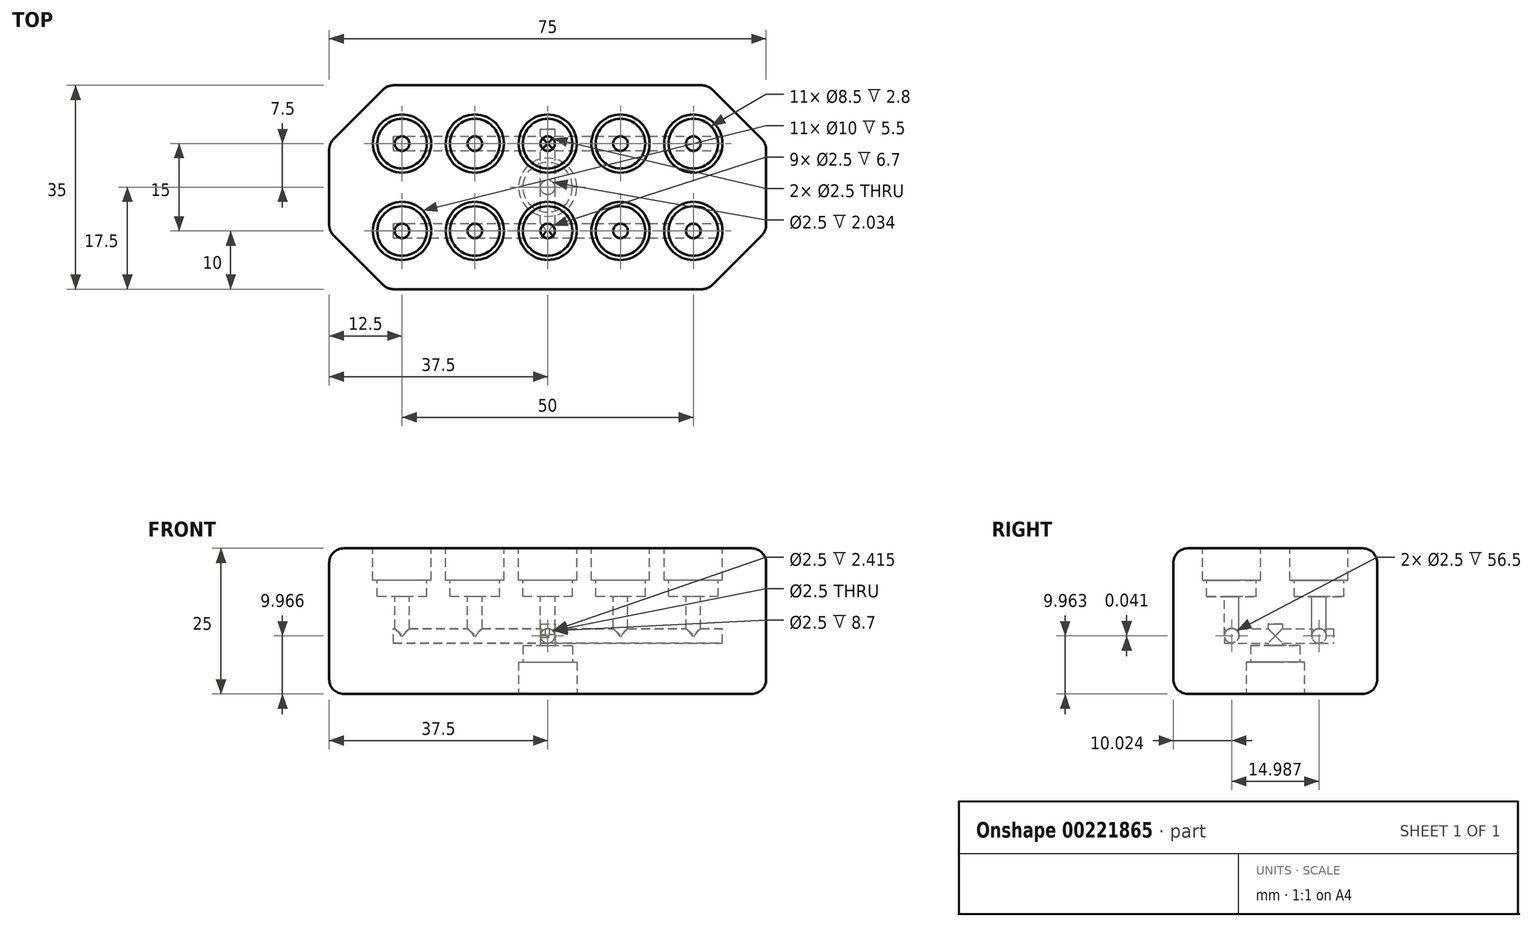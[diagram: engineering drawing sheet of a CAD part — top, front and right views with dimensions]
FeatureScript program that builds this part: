
annotation { "Feature Type Name" : "Feature", "Feature Type Description" : "" }
export const myFeature = defineFeature(function(context is Context, id is Id, definition is map)
    precondition{}
    {
        {
            var Q0;
            Q0=qCreatedBy(makeId("Top.planeOp"),FACE);
            var sketch = newSketch(context, id + "F0", { "sketchPlane" : qUnion([Q0])});
            skLineSegment(sketch, "E0.bottom", {"start": v(-37.5, 17.5) * mm, "end": v(37.5, 17.5) * mm});
            skLineSegment(sketch, "E0.top", {"start": v(-37.5, -17.5) * mm, "end": v(37.5, -17.5) * mm});
            skLineSegment(sketch, "E0.left", {"start": v(-37.5, 17.5) * mm, "end": v(-37.5, -17.5) * mm});
            skLineSegment(sketch, "E0.right", {"start": v(37.5, 17.5) * mm, "end": v(37.5, -17.5) * mm});
            skPoint(sketch, "E0.middle", {"position": v(0, 0) * mm});
            skSolve(sketch);
        }
        {
            var Q0;
            Q0=makeQuery(id+"F0.imprint","IMPRINT",FACE,{"disambiguationData":[TD([[makeQuery(id+"F0.imprint","IMPRINT",EDGE,{"derivedFrom":sQuery(id+"F0.wireOp",EDGE,"E0.bottom")}),-1.0]])]});
            extrude(context, id + "F1", {"entities" : qUnion([Q0]), "depth" : 25 * mm});
        }
        {
            var Q0;
            Q0=makeQuery(id+"F1.opExtrude","CAP_FACE",FACE,{"disambiguationData":[OSD([sQuery(id+"F0.wireOp",EDGE,"E0.bottom"),sQuery(id+"F0.wireOp",EDGE,"E0.top"),sQuery(id+"F0.wireOp",EDGE,"E0.left"),sQuery(id+"F0.wireOp",EDGE,"E0.right")])],"isStart":false});
            var sketch = newSketch(context, id + "F2", { "sketchPlane" : qUnion([Q0])});
            skCircle(sketch, "E1", {"center": v(-25, 7.5) * mm, "radius": 5 * mm});
            skCircle(sketch, "E2", {"center": v(-25, -7.5) * mm, "radius": 5 * mm});
            skCircle(sketch, "E3", {"center": v(-12.5, 7.5) * mm, "radius": 5 * mm});
            skCircle(sketch, "E4", {"center": v(-12.5, -7.5) * mm, "radius": 5 * mm});
            skCircle(sketch, "E5", {"center": v(0, 7.5) * mm, "radius": 5 * mm});
            skCircle(sketch, "E6", {"center": v(12.5, -7.5) * mm, "radius": 5 * mm});
            skCircle(sketch, "E7", {"center": v(0, -7.5) * mm, "radius": 5 * mm});
            skCircle(sketch, "E8", {"center": v(12.5, 7.5) * mm, "radius": 5 * mm});
            skCircle(sketch, "E9", {"center": v(25, -7.5) * mm, "radius": 5 * mm});
            skCircle(sketch, "E10", {"center": v(25, 7.5) * mm, "radius": 5 * mm});
            skCircle(sketch, "E11", {"center": v(-25, 7.5) * mm, "radius": 4.25 * mm});
            skCircle(sketch, "E12", {"center": v(-12.5, 7.5) * mm, "radius": 4.25 * mm});
            skCircle(sketch, "E13", {"center": v(0, 7.5) * mm, "radius": 4.25 * mm});
            skCircle(sketch, "E14", {"center": v(12.5, 7.5) * mm, "radius": 4.25 * mm});
            skCircle(sketch, "E15", {"center": v(25, 7.5) * mm, "radius": 4.25 * mm});
            skCircle(sketch, "E16", {"center": v(25, -7.5) * mm, "radius": 4.25 * mm});
            skCircle(sketch, "E17", {"center": v(12.5, -7.5) * mm, "radius": 4.25 * mm});
            skCircle(sketch, "E18", {"center": v(0, -7.5) * mm, "radius": 4.25 * mm});
            skCircle(sketch, "E19", {"center": v(-12.5, -7.5) * mm, "radius": 4.25 * mm});
            skCircle(sketch, "E20", {"center": v(-25, -7.5) * mm, "radius": 4.25 * mm});
            skCircle(sketch, "E21", {"center": v(-25, 7.5) * mm, "radius": 1.25 * mm});
            skCircle(sketch, "E22", {"center": v(-12.5, 7.5) * mm, "radius": 1.25 * mm});
            skCircle(sketch, "E23", {"center": v(0, 7.5) * mm, "radius": 1.25 * mm});
            skCircle(sketch, "E24", {"center": v(12.5, 7.5) * mm, "radius": 1.25 * mm});
            skCircle(sketch, "E25", {"center": v(25, 7.5) * mm, "radius": 1.25 * mm});
            skCircle(sketch, "E26", {"center": v(25, -7.5) * mm, "radius": 1.25 * mm});
            skCircle(sketch, "E27", {"center": v(0, -7.5) * mm, "radius": 1.25 * mm});
            skCircle(sketch, "E28", {"center": v(-25, -7.5) * mm, "radius": 1.25 * mm});
            skCircle(sketch, "E29", {"center": v(-12.5, -7.5) * mm, "radius": 1.25 * mm});
            skCircle(sketch, "E30", {"center": v(12.5, -7.5) * mm, "radius": 1.25 * mm});
            skSolve(sketch);
        }
        {
            var Q0;
            Q0=makeQuery(id+"F1.opExtrude","CAP_FACE",FACE,{"disambiguationData":[OSD([sQuery(id+"F0.wireOp",EDGE,"E0.bottom"),sQuery(id+"F0.wireOp",EDGE,"E0.top"),sQuery(id+"F0.wireOp",EDGE,"E0.left"),sQuery(id+"F0.wireOp",EDGE,"E0.right")])],"isStart":true});
            var sketch = newSketch(context, id + "F3", { "sketchPlane" : qUnion([Q0])});
            skCircle(sketch, "E31", {"center": v(0, 0) * mm, "radius": 5 * mm});
            skCircle(sketch, "E32", {"center": v(0, 0) * mm, "radius": 4.25 * mm});
            skCircle(sketch, "E33", {"center": v(0, 0) * mm, "radius": 1.25 * mm});
            skSolve(sketch);
        }
        {
            var Q0;
            Q0=makeQuery(id+"F2.imprint","IMPRINT",FACE,{"disambiguationData":[TD([[makeQuery(id+"F2.imprint","IMPRINT",EDGE,{"derivedFrom":sQuery(id+"F2.wireOp",EDGE,"E11")}),1.0]])]});
            var Q1;
            Q1=makeQuery(id+"F2.imprint","IMPRINT",FACE,{"disambiguationData":[TD([[makeQuery(id+"F2.imprint","IMPRINT",EDGE,{"derivedFrom":sQuery(id+"F2.wireOp",EDGE,"E12")}),1.0]])]});
            var Q2;
            Q2=makeQuery(id+"F2.imprint","IMPRINT",FACE,{"disambiguationData":[TD([[makeQuery(id+"F2.imprint","IMPRINT",EDGE,{"derivedFrom":sQuery(id+"F2.wireOp",EDGE,"E13")}),1.0]])]});
            var Q3;
            Q3=makeQuery(id+"F2.imprint","IMPRINT",FACE,{"disambiguationData":[TD([[makeQuery(id+"F2.imprint","IMPRINT",EDGE,{"derivedFrom":sQuery(id+"F2.wireOp",EDGE,"E14")}),1.0]])]});
            var Q4;
            Q4=makeQuery(id+"F2.imprint","IMPRINT",FACE,{"disambiguationData":[TD([[makeQuery(id+"F2.imprint","IMPRINT",EDGE,{"derivedFrom":sQuery(id+"F2.wireOp",EDGE,"E15")}),1.0]])]});
            var Q5;
            Q5=makeQuery(id+"F2.imprint","IMPRINT",FACE,{"disambiguationData":[TD([[makeQuery(id+"F2.imprint","IMPRINT",EDGE,{"derivedFrom":sQuery(id+"F2.wireOp",EDGE,"E20")}),1.0]])]});
            var Q6;
            Q6=makeQuery(id+"F2.imprint","IMPRINT",FACE,{"disambiguationData":[TD([[makeQuery(id+"F2.imprint","IMPRINT",EDGE,{"derivedFrom":sQuery(id+"F2.wireOp",EDGE,"E19")}),1.0]])]});
            var Q7;
            Q7=makeQuery(id+"F2.imprint","IMPRINT",FACE,{"disambiguationData":[TD([[makeQuery(id+"F2.imprint","IMPRINT",EDGE,{"derivedFrom":sQuery(id+"F2.wireOp",EDGE,"E18")}),1.0]])]});
            var Q8;
            Q8=makeQuery(id+"F2.imprint","IMPRINT",FACE,{"disambiguationData":[TD([[makeQuery(id+"F2.imprint","IMPRINT",EDGE,{"derivedFrom":sQuery(id+"F2.wireOp",EDGE,"E17")}),1.0]])]});
            var Q9;
            Q9=makeQuery(id+"F2.imprint","IMPRINT",FACE,{"disambiguationData":[TD([[makeQuery(id+"F2.imprint","IMPRINT",EDGE,{"derivedFrom":sQuery(id+"F2.wireOp",EDGE,"E16")}),1.0]])]});
            extrude(context, id + "F4", {"entities" : qUnion([Q0, Q1, Q2, Q3, Q4, Q5, Q6, Q7, Q8, Q9]), "operationType" : NewBodyOperationType.REMOVE, "oppositeDirection" : true, "depth" : 8.3 * mm});
        }
        {
            var Q0;
            Q0=makeQuery(id+"F4.boolean.opBoolean","SPLIT",FACE,{"disambiguationData":[TD([makeQuery(id+"F4.opExtrude","SWEPT_FACE",FACE,{"disambiguationData":[OSD([sQuery(id+"F2.wireOp",EDGE,"E21")])]})])],"derivedFrom":makeQuery(id+"F1.opExtrude","CAP_FACE",FACE,{"disambiguationData":[OSD([sQuery(id+"F0.wireOp",EDGE,"E0.bottom"),sQuery(id+"F0.wireOp",EDGE,"E0.top"),sQuery(id+"F0.wireOp",EDGE,"E0.left"),sQuery(id+"F0.wireOp",EDGE,"E0.right")])],"isStart":false})});
            var Q1;
            Q1=makeQuery(id+"F4.boolean.opBoolean","SPLIT",FACE,{"disambiguationData":[TD([makeQuery(id+"F4.opExtrude","SWEPT_FACE",FACE,{"disambiguationData":[OSD([sQuery(id+"F2.wireOp",EDGE,"E22")])]})])],"derivedFrom":makeQuery(id+"F1.opExtrude","CAP_FACE",FACE,{"disambiguationData":[OSD([sQuery(id+"F0.wireOp",EDGE,"E0.bottom"),sQuery(id+"F0.wireOp",EDGE,"E0.top"),sQuery(id+"F0.wireOp",EDGE,"E0.left"),sQuery(id+"F0.wireOp",EDGE,"E0.right")])],"isStart":false})});
            var Q2;
            Q2=makeQuery(id+"F4.boolean.opBoolean","SPLIT",FACE,{"disambiguationData":[TD([makeQuery(id+"F4.opExtrude","SWEPT_FACE",FACE,{"disambiguationData":[OSD([sQuery(id+"F2.wireOp",EDGE,"E23")])]})])],"derivedFrom":makeQuery(id+"F1.opExtrude","CAP_FACE",FACE,{"disambiguationData":[OSD([sQuery(id+"F0.wireOp",EDGE,"E0.bottom"),sQuery(id+"F0.wireOp",EDGE,"E0.top"),sQuery(id+"F0.wireOp",EDGE,"E0.left"),sQuery(id+"F0.wireOp",EDGE,"E0.right")])],"isStart":false})});
            var Q3;
            Q3=makeQuery(id+"F4.boolean.opBoolean","SPLIT",FACE,{"disambiguationData":[TD([makeQuery(id+"F4.opExtrude","SWEPT_FACE",FACE,{"disambiguationData":[OSD([sQuery(id+"F2.wireOp",EDGE,"E24")])]})])],"derivedFrom":makeQuery(id+"F1.opExtrude","CAP_FACE",FACE,{"disambiguationData":[OSD([sQuery(id+"F0.wireOp",EDGE,"E0.bottom"),sQuery(id+"F0.wireOp",EDGE,"E0.top"),sQuery(id+"F0.wireOp",EDGE,"E0.left"),sQuery(id+"F0.wireOp",EDGE,"E0.right")])],"isStart":false})});
            var Q4;
            Q4=makeQuery(id+"F4.boolean.opBoolean","SPLIT",FACE,{"disambiguationData":[TD([makeQuery(id+"F4.opExtrude","SWEPT_FACE",FACE,{"disambiguationData":[OSD([sQuery(id+"F2.wireOp",EDGE,"E25")])]})])],"derivedFrom":makeQuery(id+"F1.opExtrude","CAP_FACE",FACE,{"disambiguationData":[OSD([sQuery(id+"F0.wireOp",EDGE,"E0.bottom"),sQuery(id+"F0.wireOp",EDGE,"E0.top"),sQuery(id+"F0.wireOp",EDGE,"E0.left"),sQuery(id+"F0.wireOp",EDGE,"E0.right")])],"isStart":false})});
            var Q5;
            Q5=makeQuery(id+"F4.boolean.opBoolean","SPLIT",FACE,{"disambiguationData":[TD([makeQuery(id+"F4.opExtrude","SWEPT_FACE",FACE,{"disambiguationData":[OSD([sQuery(id+"F2.wireOp",EDGE,"E28")])]})])],"derivedFrom":makeQuery(id+"F1.opExtrude","CAP_FACE",FACE,{"disambiguationData":[OSD([sQuery(id+"F0.wireOp",EDGE,"E0.bottom"),sQuery(id+"F0.wireOp",EDGE,"E0.top"),sQuery(id+"F0.wireOp",EDGE,"E0.left"),sQuery(id+"F0.wireOp",EDGE,"E0.right")])],"isStart":false})});
            var Q6;
            Q6=makeQuery(id+"F4.boolean.opBoolean","SPLIT",FACE,{"disambiguationData":[TD([makeQuery(id+"F4.opExtrude","SWEPT_FACE",FACE,{"disambiguationData":[OSD([sQuery(id+"F2.wireOp",EDGE,"E29")])]})])],"derivedFrom":makeQuery(id+"F1.opExtrude","CAP_FACE",FACE,{"disambiguationData":[OSD([sQuery(id+"F0.wireOp",EDGE,"E0.bottom"),sQuery(id+"F0.wireOp",EDGE,"E0.top"),sQuery(id+"F0.wireOp",EDGE,"E0.left"),sQuery(id+"F0.wireOp",EDGE,"E0.right")])],"isStart":false})});
            var Q7;
            Q7=makeQuery(id+"F4.boolean.opBoolean","SPLIT",FACE,{"disambiguationData":[TD([makeQuery(id+"F4.opExtrude","SWEPT_FACE",FACE,{"disambiguationData":[OSD([sQuery(id+"F2.wireOp",EDGE,"E27")])]})])],"derivedFrom":makeQuery(id+"F1.opExtrude","CAP_FACE",FACE,{"disambiguationData":[OSD([sQuery(id+"F0.wireOp",EDGE,"E0.bottom"),sQuery(id+"F0.wireOp",EDGE,"E0.top"),sQuery(id+"F0.wireOp",EDGE,"E0.left"),sQuery(id+"F0.wireOp",EDGE,"E0.right")])],"isStart":false})});
            var Q8;
            Q8=makeQuery(id+"F4.boolean.opBoolean","SPLIT",FACE,{"disambiguationData":[TD([makeQuery(id+"F4.opExtrude","SWEPT_FACE",FACE,{"disambiguationData":[OSD([sQuery(id+"F2.wireOp",EDGE,"E30")])]})])],"derivedFrom":makeQuery(id+"F1.opExtrude","CAP_FACE",FACE,{"disambiguationData":[OSD([sQuery(id+"F0.wireOp",EDGE,"E0.bottom"),sQuery(id+"F0.wireOp",EDGE,"E0.top"),sQuery(id+"F0.wireOp",EDGE,"E0.left"),sQuery(id+"F0.wireOp",EDGE,"E0.right")])],"isStart":false})});
            var Q9;
            Q9=makeQuery(id+"F4.boolean.opBoolean","SPLIT",FACE,{"disambiguationData":[TD([makeQuery(id+"F4.opExtrude","SWEPT_FACE",FACE,{"disambiguationData":[OSD([sQuery(id+"F2.wireOp",EDGE,"E26")])]})])],"derivedFrom":makeQuery(id+"F1.opExtrude","CAP_FACE",FACE,{"disambiguationData":[OSD([sQuery(id+"F0.wireOp",EDGE,"E0.bottom"),sQuery(id+"F0.wireOp",EDGE,"E0.top"),sQuery(id+"F0.wireOp",EDGE,"E0.left"),sQuery(id+"F0.wireOp",EDGE,"E0.right")])],"isStart":false})});
            extrude(context, id + "F5", {"entities" : qUnion([Q0, Q1, Q2, Q3, Q4, Q5, Q6, Q7, Q8, Q9]), "operationType" : NewBodyOperationType.REMOVE, "oppositeDirection" : true, "depth" : 15 * mm});
        }
        {
            var Q0;
            Q0=makeQuery(id+"F2.imprint","IMPRINT",FACE,{"disambiguationData":[TD([[makeQuery(id+"F2.imprint","IMPRINT",EDGE,{"derivedFrom":sQuery(id+"F2.wireOp",EDGE,"E1")}),1.0]])]});
            var Q1;
            Q1=makeQuery(id+"F2.imprint","IMPRINT",FACE,{"disambiguationData":[TD([[makeQuery(id+"F2.imprint","IMPRINT",EDGE,{"derivedFrom":sQuery(id+"F2.wireOp",EDGE,"E3")}),1.0]])]});
            var Q2;
            Q2=makeQuery(id+"F2.imprint","IMPRINT",FACE,{"disambiguationData":[TD([[makeQuery(id+"F2.imprint","IMPRINT",EDGE,{"derivedFrom":sQuery(id+"F2.wireOp",EDGE,"E2")}),1.0]])]});
            var Q3;
            Q3=makeQuery(id+"F2.imprint","IMPRINT",FACE,{"disambiguationData":[TD([[makeQuery(id+"F2.imprint","IMPRINT",EDGE,{"derivedFrom":sQuery(id+"F2.wireOp",EDGE,"E4")}),1.0]])]});
            var Q4;
            Q4=makeQuery(id+"F2.imprint","IMPRINT",FACE,{"disambiguationData":[TD([[makeQuery(id+"F2.imprint","IMPRINT",EDGE,{"derivedFrom":sQuery(id+"F2.wireOp",EDGE,"E7")}),1.0]])]});
            var Q5;
            Q5=makeQuery(id+"F2.imprint","IMPRINT",FACE,{"disambiguationData":[TD([[makeQuery(id+"F2.imprint","IMPRINT",EDGE,{"derivedFrom":sQuery(id+"F2.wireOp",EDGE,"E6")}),1.0]])]});
            var Q6;
            Q6=makeQuery(id+"F2.imprint","IMPRINT",FACE,{"disambiguationData":[TD([[makeQuery(id+"F2.imprint","IMPRINT",EDGE,{"derivedFrom":sQuery(id+"F2.wireOp",EDGE,"E9")}),1.0]])]});
            var Q7;
            Q7=makeQuery(id+"F2.imprint","IMPRINT",FACE,{"disambiguationData":[TD([[makeQuery(id+"F2.imprint","IMPRINT",EDGE,{"derivedFrom":sQuery(id+"F2.wireOp",EDGE,"E5")}),1.0]])]});
            var Q8;
            Q8=makeQuery(id+"F2.imprint","IMPRINT",FACE,{"disambiguationData":[TD([[makeQuery(id+"F2.imprint","IMPRINT",EDGE,{"derivedFrom":sQuery(id+"F2.wireOp",EDGE,"E8")}),1.0]])]});
            var Q9;
            Q9=makeQuery(id+"F2.imprint","IMPRINT",FACE,{"disambiguationData":[TD([[makeQuery(id+"F2.imprint","IMPRINT",EDGE,{"derivedFrom":sQuery(id+"F2.wireOp",EDGE,"E10")}),1.0]])]});
            extrude(context, id + "F6", {"entities" : qUnion([Q0, Q1, Q2, Q3, Q4, Q5, Q6, Q7, Q8, Q9]), "operationType" : NewBodyOperationType.REMOVE, "oppositeDirection" : true, "depth" : 5.5 * mm});
        }
        {
            var Q0;
            Q0=makeQuery(id+"F3.imprint","IMPRINT",FACE,{"disambiguationData":[TD([[makeQuery(id+"F3.imprint","IMPRINT",EDGE,{"derivedFrom":sQuery(id+"F3.wireOp",EDGE,"E32")}),1.0]])]});
            extrude(context, id + "F7", {"entities" : qUnion([Q0]), "operationType" : NewBodyOperationType.REMOVE, "oppositeDirection" : true, "depth" : 8.3 * mm});
        }
        {
            var Q0;
            Q0=makeQuery(id+"F7.boolean.opBoolean","SPLIT",FACE,{"disambiguationData":[TD([makeQuery(id+"F7.opExtrude","SWEPT_FACE",FACE,{"disambiguationData":[OSD([sQuery(id+"F3.wireOp",EDGE,"E33")])]})])],"derivedFrom":makeQuery(id+"F1.opExtrude","CAP_FACE",FACE,{"disambiguationData":[OSD([sQuery(id+"F0.wireOp",EDGE,"E0.bottom"),sQuery(id+"F0.wireOp",EDGE,"E0.top"),sQuery(id+"F0.wireOp",EDGE,"E0.left"),sQuery(id+"F0.wireOp",EDGE,"E0.right")])],"isStart":true})});
            extrude(context, id + "F8", {"entities" : qUnion([Q0]), "operationType" : NewBodyOperationType.REMOVE, "oppositeDirection" : true, "depth" : 12 * mm});
        }
        {
            var Q0;
            Q0=makeQuery(id+"F3.imprint","IMPRINT",FACE,{"disambiguationData":[TD([[makeQuery(id+"F3.imprint","IMPRINT",EDGE,{"derivedFrom":sQuery(id+"F3.wireOp",EDGE,"E31")}),1.0]])]});
            extrude(context, id + "F9", {"entities" : qUnion([Q0]), "operationType" : NewBodyOperationType.REMOVE, "oppositeDirection" : true, "depth" : 5.5 * mm});
        }
        {
            var Q0;
            Q0=makeQuery(id+"F1.opExtrude","SWEPT_FACE",FACE,{"disambiguationData":[OSD([sQuery(id+"F0.wireOp",EDGE,"E0.right")])]});
            var sketch = newSketch(context, id + "F10", { "sketchPlane" : qUnion([Q0])});
            skCircle(sketch, "E34", {"center": v(-7.48, 10) * mm, "radius": 1.25 * mm});
            skCircle(sketch, "E35", {"center": v(7.51, 9.96) * mm, "radius": 1.25 * mm});
            skSolve(sketch);
        }
        {
            var Q0;
            Q0=makeQuery(id+"F10.imprint","IMPRINT",FACE,{"disambiguationData":[TD([[makeQuery(id+"F10.imprint","IMPRINT",EDGE,{"derivedFrom":sQuery(id+"F10.wireOp",EDGE,"E35")}),1.0]])]});
            var Q1;
            Q1=makeQuery(id+"F10.imprint","IMPRINT",FACE,{"disambiguationData":[TD([[makeQuery(id+"F10.imprint","IMPRINT",EDGE,{"derivedFrom":sQuery(id+"F10.wireOp",EDGE,"E34")}),1.0]])]});
            extrude(context, id + "F11", {"entities" : qUnion([Q0, Q1]), "operationType" : NewBodyOperationType.REMOVE, "oppositeDirection" : true, "depth" : 64 * mm});
        }
        {
            var Q0;
            Q0=makeQuery(id+"F1.opExtrude","SWEPT_FACE",FACE,{"disambiguationData":[OSD([sQuery(id+"F0.wireOp",EDGE,"E0.bottom")])]});
            var sketch = newSketch(context, id + "F12", { "sketchPlane" : qUnion([Q0])});
            skCircle(sketch, "E36", {"center": v(0, 9.97) * mm, "radius": 1.25 * mm});
            skSolve(sketch);
        }
        {
            var Q0;
            Q0=makeQuery(id+"F12.imprint","IMPRINT",FACE,{"disambiguationData":[TD([[makeQuery(id+"F12.imprint","IMPRINT",EDGE,{"derivedFrom":sQuery(id+"F12.wireOp",EDGE,"E36")}),1.0]])]});
            extrude(context, id + "F13", {"entities" : qUnion([Q0]), "operationType" : NewBodyOperationType.REMOVE, "oppositeDirection" : true, "depth" : 26.2 * mm});
        }
        {
            var Q0;
            Q0=makeQuery(id+"F1.opExtrude","SWEPT_FACE",FACE,{"disambiguationData":[OSD([sQuery(id+"F0.wireOp",EDGE,"E0.right")])]});
            var sketch = newSketch(context, id + "F14", { "sketchPlane" : qUnion([Q0])});
            skCircle(sketch, "E37", {"center": v(-7.48, 10) * mm, "radius": 1.25 * mm});
            skCircle(sketch, "E38", {"center": v(7.51, 9.96) * mm, "radius": 1.25 * mm});
            skSolve(sketch);
        }
        {
            var Q0;
            Q0 = qSketchRegion(id + "F14", true);
            extrude(context, id + "F15", {"entities" : qUnion([Q0]), "operationType" : NewBodyOperationType.ADD, "oppositeDirection" : true, "depth" : 7.5 * mm});
        }
        {
            var Q0;
            Q0=makeQuery(id+"F1.opExtrude","SWEPT_FACE",FACE,{"disambiguationData":[OSD([sQuery(id+"F0.wireOp",EDGE,"E0.bottom")])]});
            var sketch = newSketch(context, id + "F16", { "sketchPlane" : qUnion([Q0])});
            skCircle(sketch, "E39", {"center": v(0, 9.97) * mm, "radius": 1.25 * mm});
            skSolve(sketch);
        }
        {
            var Q0;
            Q0 = qSketchRegion(id + "F16", true);
            extrude(context, id + "F17", {"entities" : qUnion([Q0]), "operationType" : NewBodyOperationType.ADD, "oppositeDirection" : true, "depth" : 7.5 * mm});
        }
        {
            var Q0;
            Q0=makeQuery(id+"F1.opExtrude","SWEPT_EDGE",EDGE,{"disambiguationData":[OSD([sQuery(id+"F0.wireOp",EDGE,"E0.bottom"),sQuery(id+"F0.wireOp",EDGE,"E0.left")])]});
            var Q1;
            Q1=makeQuery(id+"F1.opExtrude","SWEPT_EDGE",EDGE,{"disambiguationData":[OSD([sQuery(id+"F0.wireOp",EDGE,"E0.top"),sQuery(id+"F0.wireOp",EDGE,"E0.left")])]});
            var Q2;
            Q2=makeQuery(id+"F1.opExtrude","SWEPT_EDGE",EDGE,{"disambiguationData":[OSD([sQuery(id+"F0.wireOp",EDGE,"E0.top"),sQuery(id+"F0.wireOp",EDGE,"E0.right")])]});
            var Q3;
            Q3=makeQuery(id+"F1.opExtrude","SWEPT_EDGE",EDGE,{"disambiguationData":[OSD([sQuery(id+"F0.wireOp",EDGE,"E0.bottom"),sQuery(id+"F0.wireOp",EDGE,"E0.right")])]});
            chamfer(context, id + "F18", {"entities" : qUnion([Q0, Q1, Q2, Q3]), "width" : 10 * mm, "tangentPropagation" : true});
        }
        {
            var Q0;
            {var subQ0=sQuery(id+"F0.wireOp",EDGE,"E0.left");Q0=makeQuery(id+"F18.opChamfer","BLEND_EDGE",EDGE,{"blendedFrom":[makeQuery(id+"F1.opExtrude","SWEPT_EDGE",EDGE,{"disambiguationData":[OSD([sQuery(id+"F0.wireOp",EDGE,"E0.bottom"),subQ0])]}),makeQuery(id+"F1.opExtrude","SWEPT_FACE",FACE,{"disambiguationData":[OSD([subQ0])]})],"blendedInto":[makeQuery(id+"F1.opExtrude","SWEPT_FACE",FACE,{"disambiguationData":[OSD([subQ0])]})]});}
            var Q1;
            {var subQ0=sQuery(id+"F0.wireOp",EDGE,"E0.left");Q1=makeQuery(id+"F18.opChamfer","BLEND_EDGE",EDGE,{"blendedFrom":[makeQuery(id+"F1.opExtrude","SWEPT_EDGE",EDGE,{"disambiguationData":[OSD([sQuery(id+"F0.wireOp",EDGE,"E0.top"),subQ0])]}),makeQuery(id+"F1.opExtrude","SWEPT_FACE",FACE,{"disambiguationData":[OSD([subQ0])]})],"blendedInto":[makeQuery(id+"F1.opExtrude","SWEPT_FACE",FACE,{"disambiguationData":[OSD([subQ0])]})]});}
            var Q2;
            {var subQ0=sQuery(id+"F0.wireOp",EDGE,"E0.bottom");var subQ1=sQuery(id+"F0.wireOp",EDGE,"E0.top");var subQ2=sQuery(id+"F0.wireOp",EDGE,"E0.left");var subQ3=sQuery(id+"F0.wireOp",EDGE,"E0.right");Q2=makeQuery(id+"F18.opChamfer","BLEND_EDGE",EDGE,{"blendedFrom":[makeQuery(id+"F1.opExtrude","SWEPT_EDGE",EDGE,{"disambiguationData":[OSD([subQ1,subQ3])]}),makeQuery(id+"F4.boolean.opBoolean","SPLIT",FACE,{"disambiguationData":[TD([makeQuery(id+"F1.opExtrude","SWEPT_FACE",FACE,{"disambiguationData":[OSD([subQ0])]})])],"derivedFrom":makeQuery(id+"F1.opExtrude","CAP_FACE",FACE,{"disambiguationData":[OSD([subQ0,subQ1,subQ2,subQ3])],"isStart":false})})],"blendedInto":[makeQuery(id+"F4.boolean.opBoolean","SPLIT",FACE,{"disambiguationData":[TD([makeQuery(id+"F1.opExtrude","SWEPT_FACE",FACE,{"disambiguationData":[OSD([subQ0])]})])],"derivedFrom":makeQuery(id+"F1.opExtrude","CAP_FACE",FACE,{"disambiguationData":[OSD([subQ0,subQ1,subQ2,subQ3])],"isStart":false})})]});}
            var Q3;
            {var subQ0=sQuery(id+"F0.wireOp",EDGE,"E0.bottom");Q3=makeQuery(id+"F18.opChamfer","BLEND_EDGE",EDGE,{"blendedFrom":[makeQuery(id+"F1.opExtrude","SWEPT_EDGE",EDGE,{"disambiguationData":[OSD([subQ0,sQuery(id+"F0.wireOp",EDGE,"E0.left")])]}),makeQuery(id+"F17.boolean.opBoolean","MERGE",FACE,{"derivedFrom":[makeQuery(id+"F1.opExtrude","SWEPT_FACE",FACE,{"disambiguationData":[OSD([subQ0])]}),makeQuery(id+"F17.opExtrude","CAP_FACE",FACE,{"disambiguationData":[OSD([sQuery(id+"F16.wireOp",EDGE,"E39")])],"isStart":true})]})],"blendedInto":[makeQuery(id+"F17.boolean.opBoolean","MERGE",FACE,{"derivedFrom":[makeQuery(id+"F1.opExtrude","SWEPT_FACE",FACE,{"disambiguationData":[OSD([subQ0])]}),makeQuery(id+"F17.opExtrude","CAP_FACE",FACE,{"disambiguationData":[OSD([sQuery(id+"F16.wireOp",EDGE,"E39")])],"isStart":true})]})]});}
            var Q4;
            {var subQ0=sQuery(id+"F0.wireOp",EDGE,"E0.bottom");var subQ1=sQuery(id+"F0.wireOp",EDGE,"E0.top");var subQ2=sQuery(id+"F0.wireOp",EDGE,"E0.left");var subQ3=sQuery(id+"F0.wireOp",EDGE,"E0.right");Q4=makeQuery(id+"F18.opChamfer","BLEND_EDGE",EDGE,{"blendedFrom":[makeQuery(id+"F1.opExtrude","SWEPT_EDGE",EDGE,{"disambiguationData":[OSD([subQ0,subQ2])]}),makeQuery(id+"F4.boolean.opBoolean","SPLIT",FACE,{"disambiguationData":[TD([makeQuery(id+"F1.opExtrude","SWEPT_FACE",FACE,{"disambiguationData":[OSD([subQ0])]})])],"derivedFrom":makeQuery(id+"F1.opExtrude","CAP_FACE",FACE,{"disambiguationData":[OSD([subQ0,subQ1,subQ2,subQ3])],"isStart":false})})],"blendedInto":[makeQuery(id+"F4.boolean.opBoolean","SPLIT",FACE,{"disambiguationData":[TD([makeQuery(id+"F1.opExtrude","SWEPT_FACE",FACE,{"disambiguationData":[OSD([subQ0])]})])],"derivedFrom":makeQuery(id+"F1.opExtrude","CAP_FACE",FACE,{"disambiguationData":[OSD([subQ0,subQ1,subQ2,subQ3])],"isStart":false})})]});}
            var Q5;
            {var subQ0=sQuery(id+"F0.wireOp",EDGE,"E0.right");var subQ1=sQuery(id+"F0.wireOp",EDGE,"E0.left");var subQ2=sQuery(id+"F0.wireOp",EDGE,"E0.top");var subQ3=sQuery(id+"F0.wireOp",EDGE,"E0.bottom");Q5=makeQuery(id+"F18.opChamfer","BLEND_EDGE",EDGE,{"blendedFrom":[makeQuery(id+"F1.opExtrude","SWEPT_EDGE",EDGE,{"disambiguationData":[OSD([subQ3,subQ1])]}),makeQuery(id+"F7.boolean.opBoolean","SPLIT",FACE,{"disambiguationData":[TD([makeQuery(id+"F1.opExtrude","SWEPT_FACE",FACE,{"disambiguationData":[OSD([subQ3])]})])],"derivedFrom":makeQuery(id+"F1.opExtrude","CAP_FACE",FACE,{"disambiguationData":[OSD([subQ3,subQ2,subQ1,subQ0])],"isStart":true})})],"blendedInto":[makeQuery(id+"F7.boolean.opBoolean","SPLIT",FACE,{"disambiguationData":[TD([makeQuery(id+"F1.opExtrude","SWEPT_FACE",FACE,{"disambiguationData":[OSD([subQ3])]})])],"derivedFrom":makeQuery(id+"F1.opExtrude","CAP_FACE",FACE,{"disambiguationData":[OSD([subQ3,subQ2,subQ1,subQ0])],"isStart":true})})]});}
            var Q6;
            Q6=makeQuery(id+"F1.opExtrude","CAP_EDGE",EDGE,{"disambiguationData":[OSD([sQuery(id+"F0.wireOp",EDGE,"E0.left")])],"isStart":false});
            var Q7;
            Q7=makeQuery(id+"F1.opExtrude","CAP_EDGE",EDGE,{"disambiguationData":[OSD([sQuery(id+"F0.wireOp",EDGE,"E0.left")])],"isStart":true});
            var Q8;
            Q8=makeQuery(id+"F1.opExtrude","CAP_EDGE",EDGE,{"disambiguationData":[OSD([sQuery(id+"F0.wireOp",EDGE,"E0.bottom")])],"isStart":false});
            var Q9;
            Q9=makeQuery(id+"F1.opExtrude","CAP_EDGE",EDGE,{"disambiguationData":[OSD([sQuery(id+"F0.wireOp",EDGE,"E0.bottom")])],"isStart":true});
            var Q10;
            Q10=makeQuery(id+"F1.opExtrude","CAP_EDGE",EDGE,{"disambiguationData":[OSD([sQuery(id+"F0.wireOp",EDGE,"E0.top")])],"isStart":false});
            var Q11;
            {var subQ0=sQuery(id+"F0.wireOp",EDGE,"E0.bottom");var subQ1=sQuery(id+"F0.wireOp",EDGE,"E0.top");var subQ2=sQuery(id+"F0.wireOp",EDGE,"E0.left");var subQ3=sQuery(id+"F0.wireOp",EDGE,"E0.right");Q11=makeQuery(id+"F18.opChamfer","BLEND_EDGE",EDGE,{"blendedFrom":[makeQuery(id+"F1.opExtrude","SWEPT_EDGE",EDGE,{"disambiguationData":[OSD([subQ1,subQ2])]}),makeQuery(id+"F4.boolean.opBoolean","SPLIT",FACE,{"disambiguationData":[TD([makeQuery(id+"F1.opExtrude","SWEPT_FACE",FACE,{"disambiguationData":[OSD([subQ0])]})])],"derivedFrom":makeQuery(id+"F1.opExtrude","CAP_FACE",FACE,{"disambiguationData":[OSD([subQ0,subQ1,subQ2,subQ3])],"isStart":false})})],"blendedInto":[makeQuery(id+"F4.boolean.opBoolean","SPLIT",FACE,{"disambiguationData":[TD([makeQuery(id+"F1.opExtrude","SWEPT_FACE",FACE,{"disambiguationData":[OSD([subQ0])]})])],"derivedFrom":makeQuery(id+"F1.opExtrude","CAP_FACE",FACE,{"disambiguationData":[OSD([subQ0,subQ1,subQ2,subQ3])],"isStart":false})})]});}
            var Q12;
            {var subQ0=sQuery(id+"F0.wireOp",EDGE,"E0.top");Q12=makeQuery(id+"F18.opChamfer","BLEND_EDGE",EDGE,{"blendedFrom":[makeQuery(id+"F1.opExtrude","SWEPT_EDGE",EDGE,{"disambiguationData":[OSD([subQ0,sQuery(id+"F0.wireOp",EDGE,"E0.left")])]}),makeQuery(id+"F1.opExtrude","SWEPT_FACE",FACE,{"disambiguationData":[OSD([subQ0])]})],"blendedInto":[makeQuery(id+"F1.opExtrude","SWEPT_FACE",FACE,{"disambiguationData":[OSD([subQ0])]})]});}
            var Q13;
            {var subQ0=sQuery(id+"F0.wireOp",EDGE,"E0.right");var subQ1=sQuery(id+"F0.wireOp",EDGE,"E0.left");var subQ2=sQuery(id+"F0.wireOp",EDGE,"E0.top");var subQ3=sQuery(id+"F0.wireOp",EDGE,"E0.bottom");Q13=makeQuery(id+"F18.opChamfer","BLEND_EDGE",EDGE,{"blendedFrom":[makeQuery(id+"F1.opExtrude","SWEPT_EDGE",EDGE,{"disambiguationData":[OSD([subQ2,subQ1])]}),makeQuery(id+"F7.boolean.opBoolean","SPLIT",FACE,{"disambiguationData":[TD([makeQuery(id+"F1.opExtrude","SWEPT_FACE",FACE,{"disambiguationData":[OSD([subQ3])]})])],"derivedFrom":makeQuery(id+"F1.opExtrude","CAP_FACE",FACE,{"disambiguationData":[OSD([subQ3,subQ2,subQ1,subQ0])],"isStart":true})})],"blendedInto":[makeQuery(id+"F7.boolean.opBoolean","SPLIT",FACE,{"disambiguationData":[TD([makeQuery(id+"F1.opExtrude","SWEPT_FACE",FACE,{"disambiguationData":[OSD([subQ3])]})])],"derivedFrom":makeQuery(id+"F1.opExtrude","CAP_FACE",FACE,{"disambiguationData":[OSD([subQ3,subQ2,subQ1,subQ0])],"isStart":true})})]});}
            var Q14;
            {var subQ0=sQuery(id+"F0.wireOp",EDGE,"E0.top");Q14=makeQuery(id+"F18.opChamfer","BLEND_EDGE",EDGE,{"blendedFrom":[makeQuery(id+"F1.opExtrude","SWEPT_EDGE",EDGE,{"disambiguationData":[OSD([subQ0,sQuery(id+"F0.wireOp",EDGE,"E0.right")])]}),makeQuery(id+"F1.opExtrude","SWEPT_FACE",FACE,{"disambiguationData":[OSD([subQ0])]})],"blendedInto":[makeQuery(id+"F1.opExtrude","SWEPT_FACE",FACE,{"disambiguationData":[OSD([subQ0])]})]});}
            var Q15;
            {var subQ0=sQuery(id+"F0.wireOp",EDGE,"E0.right");Q15=makeQuery(id+"F18.opChamfer","BLEND_EDGE",EDGE,{"blendedFrom":[makeQuery(id+"F1.opExtrude","SWEPT_EDGE",EDGE,{"disambiguationData":[OSD([sQuery(id+"F0.wireOp",EDGE,"E0.top"),subQ0])]}),makeQuery(id+"F15.boolean.opBoolean","MERGE",FACE,{"derivedFrom":[makeQuery(id+"F1.opExtrude","SWEPT_FACE",FACE,{"disambiguationData":[OSD([subQ0])]}),makeQuery(id+"F15.opExtrude","CAP_FACE",FACE,{"disambiguationData":[OSD([sQuery(id+"F14.wireOp",EDGE,"E37")])],"isStart":true}),makeQuery(id+"F15.opExtrude","CAP_FACE",FACE,{"disambiguationData":[OSD([sQuery(id+"F14.wireOp",EDGE,"E38")])],"isStart":true})]})],"blendedInto":[makeQuery(id+"F15.boolean.opBoolean","MERGE",FACE,{"derivedFrom":[makeQuery(id+"F1.opExtrude","SWEPT_FACE",FACE,{"disambiguationData":[OSD([subQ0])]}),makeQuery(id+"F15.opExtrude","CAP_FACE",FACE,{"disambiguationData":[OSD([sQuery(id+"F14.wireOp",EDGE,"E37")])],"isStart":true}),makeQuery(id+"F15.opExtrude","CAP_FACE",FACE,{"disambiguationData":[OSD([sQuery(id+"F14.wireOp",EDGE,"E38")])],"isStart":true})]})]});}
            var Q16;
            {var subQ0=sQuery(id+"F0.wireOp",EDGE,"E0.right");var subQ1=sQuery(id+"F0.wireOp",EDGE,"E0.left");var subQ2=sQuery(id+"F0.wireOp",EDGE,"E0.top");var subQ3=sQuery(id+"F0.wireOp",EDGE,"E0.bottom");Q16=makeQuery(id+"F18.opChamfer","BLEND_EDGE",EDGE,{"blendedFrom":[makeQuery(id+"F1.opExtrude","SWEPT_EDGE",EDGE,{"disambiguationData":[OSD([subQ2,subQ0])]}),makeQuery(id+"F7.boolean.opBoolean","SPLIT",FACE,{"disambiguationData":[TD([makeQuery(id+"F1.opExtrude","SWEPT_FACE",FACE,{"disambiguationData":[OSD([subQ3])]})])],"derivedFrom":makeQuery(id+"F1.opExtrude","CAP_FACE",FACE,{"disambiguationData":[OSD([subQ3,subQ2,subQ1,subQ0])],"isStart":true})})],"blendedInto":[makeQuery(id+"F7.boolean.opBoolean","SPLIT",FACE,{"disambiguationData":[TD([makeQuery(id+"F1.opExtrude","SWEPT_FACE",FACE,{"disambiguationData":[OSD([subQ3])]})])],"derivedFrom":makeQuery(id+"F1.opExtrude","CAP_FACE",FACE,{"disambiguationData":[OSD([subQ3,subQ2,subQ1,subQ0])],"isStart":true})})]});}
            var Q17;
            Q17=makeQuery(id+"F1.opExtrude","CAP_EDGE",EDGE,{"disambiguationData":[OSD([sQuery(id+"F0.wireOp",EDGE,"E0.top")])],"isStart":true});
            var Q18;
            Q18=makeQuery(id+"F1.opExtrude","CAP_EDGE",EDGE,{"disambiguationData":[OSD([sQuery(id+"F0.wireOp",EDGE,"E0.right")])],"isStart":false});
            var Q19;
            {var subQ0=sQuery(id+"F0.wireOp",EDGE,"E0.bottom");var subQ1=sQuery(id+"F0.wireOp",EDGE,"E0.top");var subQ2=sQuery(id+"F0.wireOp",EDGE,"E0.left");var subQ3=sQuery(id+"F0.wireOp",EDGE,"E0.right");Q19=makeQuery(id+"F18.opChamfer","BLEND_EDGE",EDGE,{"blendedFrom":[makeQuery(id+"F1.opExtrude","SWEPT_EDGE",EDGE,{"disambiguationData":[OSD([subQ0,subQ3])]}),makeQuery(id+"F4.boolean.opBoolean","SPLIT",FACE,{"disambiguationData":[TD([makeQuery(id+"F1.opExtrude","SWEPT_FACE",FACE,{"disambiguationData":[OSD([subQ0])]})])],"derivedFrom":makeQuery(id+"F1.opExtrude","CAP_FACE",FACE,{"disambiguationData":[OSD([subQ0,subQ1,subQ2,subQ3])],"isStart":false})})],"blendedInto":[makeQuery(id+"F4.boolean.opBoolean","SPLIT",FACE,{"disambiguationData":[TD([makeQuery(id+"F1.opExtrude","SWEPT_FACE",FACE,{"disambiguationData":[OSD([subQ0])]})])],"derivedFrom":makeQuery(id+"F1.opExtrude","CAP_FACE",FACE,{"disambiguationData":[OSD([subQ0,subQ1,subQ2,subQ3])],"isStart":false})})]});}
            var Q20;
            {var subQ0=sQuery(id+"F0.wireOp",EDGE,"E0.right");Q20=makeQuery(id+"F18.opChamfer","BLEND_EDGE",EDGE,{"blendedFrom":[makeQuery(id+"F1.opExtrude","SWEPT_EDGE",EDGE,{"disambiguationData":[OSD([sQuery(id+"F0.wireOp",EDGE,"E0.bottom"),subQ0])]}),makeQuery(id+"F15.boolean.opBoolean","MERGE",FACE,{"derivedFrom":[makeQuery(id+"F1.opExtrude","SWEPT_FACE",FACE,{"disambiguationData":[OSD([subQ0])]}),makeQuery(id+"F15.opExtrude","CAP_FACE",FACE,{"disambiguationData":[OSD([sQuery(id+"F14.wireOp",EDGE,"E37")])],"isStart":true}),makeQuery(id+"F15.opExtrude","CAP_FACE",FACE,{"disambiguationData":[OSD([sQuery(id+"F14.wireOp",EDGE,"E38")])],"isStart":true})]})],"blendedInto":[makeQuery(id+"F15.boolean.opBoolean","MERGE",FACE,{"derivedFrom":[makeQuery(id+"F1.opExtrude","SWEPT_FACE",FACE,{"disambiguationData":[OSD([subQ0])]}),makeQuery(id+"F15.opExtrude","CAP_FACE",FACE,{"disambiguationData":[OSD([sQuery(id+"F14.wireOp",EDGE,"E37")])],"isStart":true}),makeQuery(id+"F15.opExtrude","CAP_FACE",FACE,{"disambiguationData":[OSD([sQuery(id+"F14.wireOp",EDGE,"E38")])],"isStart":true})]})]});}
            var Q21;
            Q21=makeQuery(id+"F18.opChamfer","BLEND_FACE",FACE,{"disambiguationData":[OSD([sQuery(id+"F0.wireOp",EDGE,"E0.bottom"),sQuery(id+"F0.wireOp",EDGE,"E0.right")])]});
            var Q22;
            Q22=makeQuery(id+"F1.opExtrude","CAP_EDGE",EDGE,{"disambiguationData":[OSD([sQuery(id+"F0.wireOp",EDGE,"E0.right")])],"isStart":true});
            fillet(context, id + "F19", {"entities" : qUnion([Q0, Q1, Q2, Q3, Q4, Q5, Q6, Q7, Q8, Q9, Q10, Q11, Q12, Q13, Q14, Q15, Q16, Q17, Q18, Q19, Q20, Q21, Q22]), "radius" : 2.5 * mm, "tangentPropagation" : true, "allowEdgeOverflow" : false});
        }
    });
